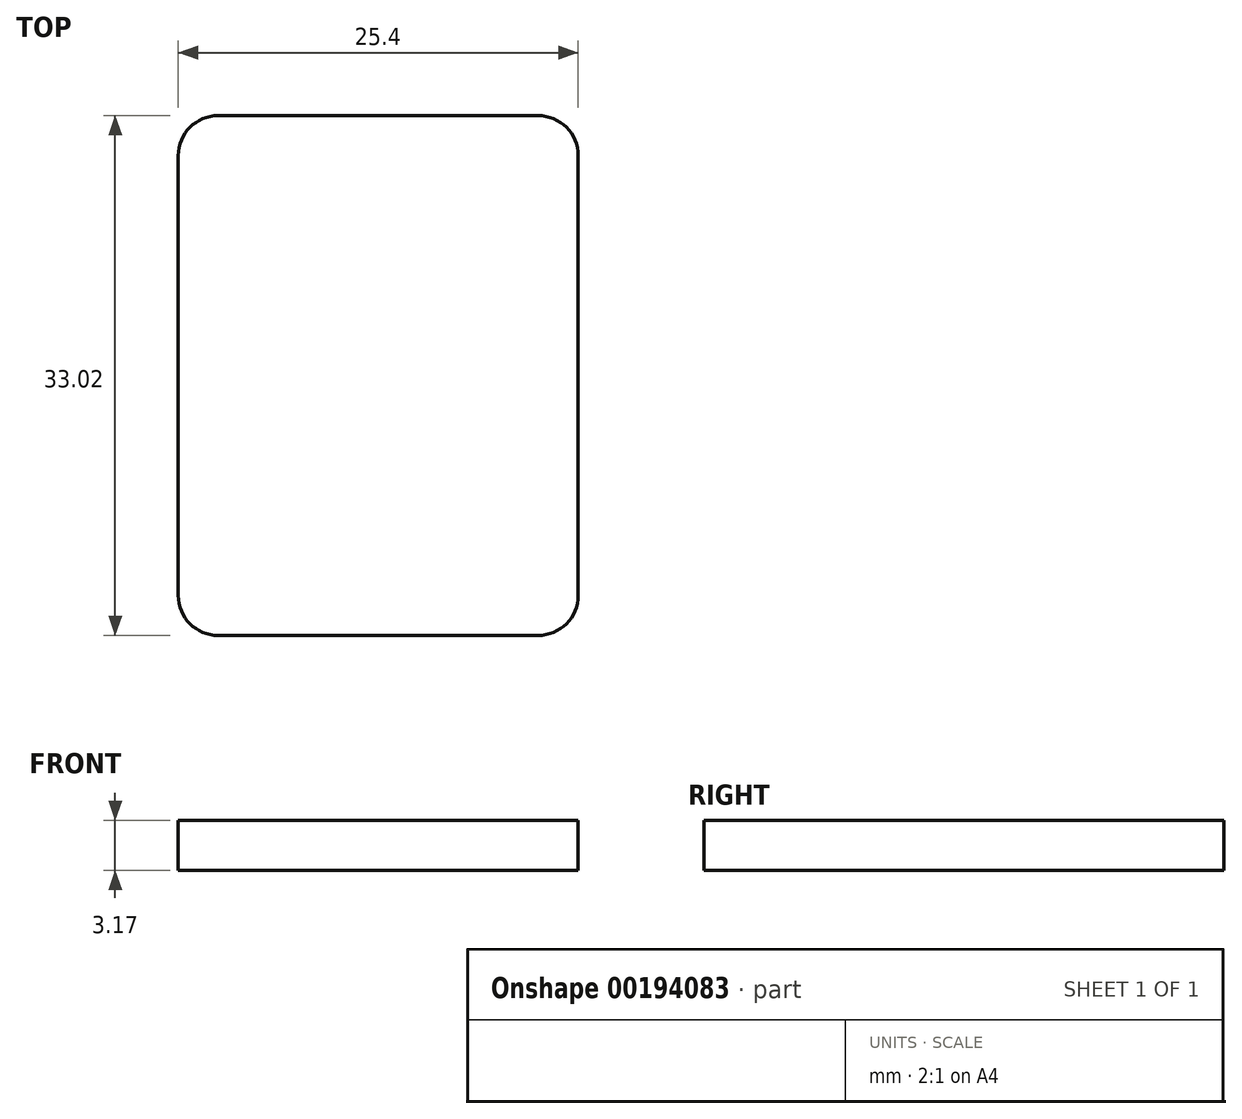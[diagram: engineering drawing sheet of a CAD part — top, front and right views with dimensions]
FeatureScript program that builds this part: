
annotation { "Feature Type Name" : "Feature", "Feature Type Description" : "" }
export const myFeature = defineFeature(function(context is Context, id is Id, definition is map)
    precondition{}
    {
        {
            var Q0;
            Q0=qCreatedBy(makeId("Top.planeOp"),FACE);
            var sketch = newSketch(context, id + "F0", { "sketchPlane" : qUnion([Q0])});
            skLineSegment(sketch, "E0.bottom", {"start": v(0, 0) * mm, "end": v(25.4, 0) * mm});
            skLineSegment(sketch, "E0.top", {"start": v(0, 33.02) * mm, "end": v(25.4, 33.02) * mm});
            skLineSegment(sketch, "E0.left", {"start": v(0, 0) * mm, "end": v(0, 33.02) * mm});
            skLineSegment(sketch, "E0.right", {"start": v(25.4, 0) * mm, "end": v(25.4, 33.02) * mm});
            skSolve(sketch);
        }
        {
            var Q0;
            Q0=qSketchRegion(id+"F0",true);
            extrude(context, id + "F1", {"entities" : qUnion([Q0]), "depth" : 3.17 * mm});
        }
        {
            var Q0;
            Q0=makeQuery(id+"F1.opExtrude","SWEPT_EDGE",EDGE,{"disambiguationData":[OSD([sQuery(id+"F0.wireOp",EDGE,"E0.bottom"),sQuery(id+"F0.wireOp",EDGE,"E0.left")])]});
            var Q1;
            Q1=makeQuery(id+"F1.opExtrude","SWEPT_EDGE",EDGE,{"disambiguationData":[OSD([sQuery(id+"F0.wireOp",EDGE,"E0.bottom"),sQuery(id+"F0.wireOp",EDGE,"E0.right")])]});
            var Q2;
            Q2=makeQuery(id+"F1.opExtrude","SWEPT_EDGE",EDGE,{"disambiguationData":[OSD([sQuery(id+"F0.wireOp",EDGE,"E0.top"),sQuery(id+"F0.wireOp",EDGE,"E0.right")])]});
            var Q3;
            Q3=makeQuery(id+"F1.opExtrude","SWEPT_EDGE",EDGE,{"disambiguationData":[OSD([sQuery(id+"F0.wireOp",EDGE,"E0.top"),sQuery(id+"F0.wireOp",EDGE,"E0.left")])]});
            fillet(context, id + "F2", {"entities" : qUnion([Q0, Q1, Q2, Q3]), "radius" : 2.54 * mm, "tangentPropagation" : true, "allowEdgeOverflow" : false});
        }
    });
